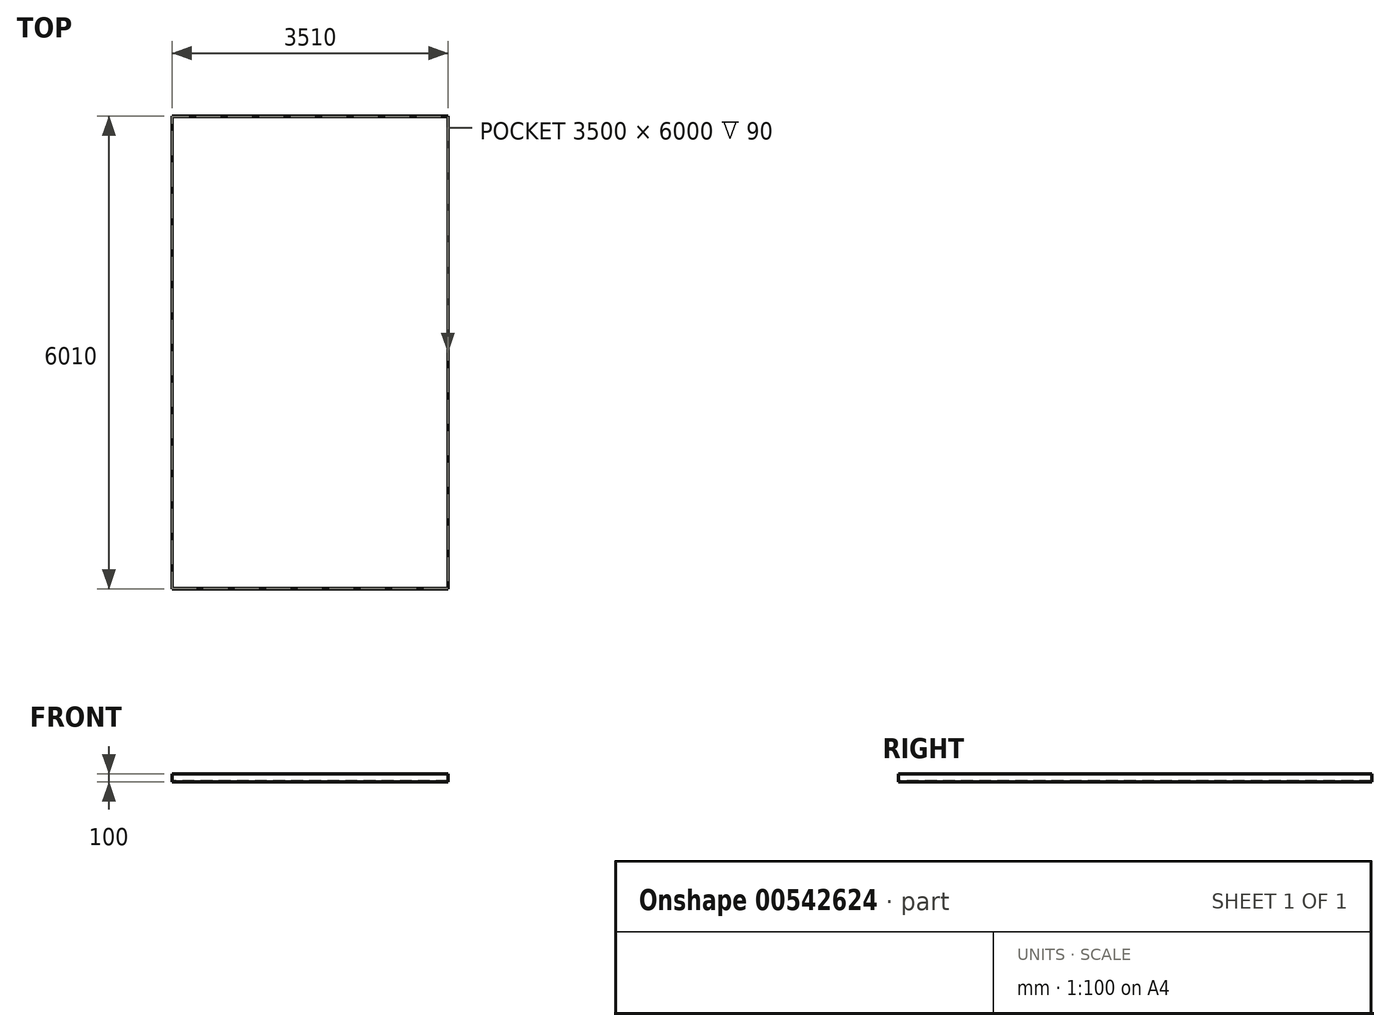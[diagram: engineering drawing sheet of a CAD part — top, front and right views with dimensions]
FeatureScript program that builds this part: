
annotation { "Feature Type Name" : "Feature", "Feature Type Description" : "" }
export const myFeature = defineFeature(function(context is Context, id is Id, definition is map)
    precondition{}
    {
        {
            var Q0;
            Q0=qCreatedBy(makeId("Top.planeOp"),FACE);
            var sketch = newSketch(context, id + "F0", { "sketchPlane" : qUnion([Q0])});
            skLineSegment(sketch, "E0.bottom", {"start": v(3500, 6000) * mm, "end": v(0, 6000) * mm});
            skLineSegment(sketch, "E0.top", {"start": v(3500, 0) * mm, "end": v(0, 0) * mm});
            skLineSegment(sketch, "E0.left", {"start": v(3500, 6000) * mm, "end": v(3500, 0) * mm});
            skLineSegment(sketch, "E0.right", {"start": v(0, 6000) * mm, "end": v(0, 0) * mm});
            skLineSegment(sketch, "E1.0", {"start": v(-5, 6005) * mm, "end": v(-5, -5) * mm});
            skLineSegment(sketch, "E1.1", {"start": v(3505, 6005) * mm, "end": v(-5, 6005) * mm});
            skLineSegment(sketch, "E1.2", {"start": v(3505, 6005) * mm, "end": v(3505, -5) * mm});
            skLineSegment(sketch, "E1.3", {"start": v(3505, -5) * mm, "end": v(-5, -5) * mm});
            skSolve(sketch);
        }
        {
            var Q0;
            Q0 = qSketchRegion(id + "F0", true);
            extrude(context, id + "F1", {"entities" : qUnion([Q0]), "depth" : 100 * mm, "offsetDistance" : 25 * mm});
        }
        {
            var Q0;
            Q0=makeQuery(id+"F0.imprint","IMPRINT",FACE,{"disambiguationData":[TD([[makeQuery(id+"F0.imprint","IMPRINT",EDGE,{"derivedFrom":sQuery(id+"F0.wireOp",EDGE,"E0.bottom")}),1.0]])]});
            extrude(context, id + "F2", {"entities" : qUnion([Q0]), "operationType" : NewBodyOperationType.ADD, "depth" : 10 * mm, "offsetDistance" : 25 * mm});
        }
    });
